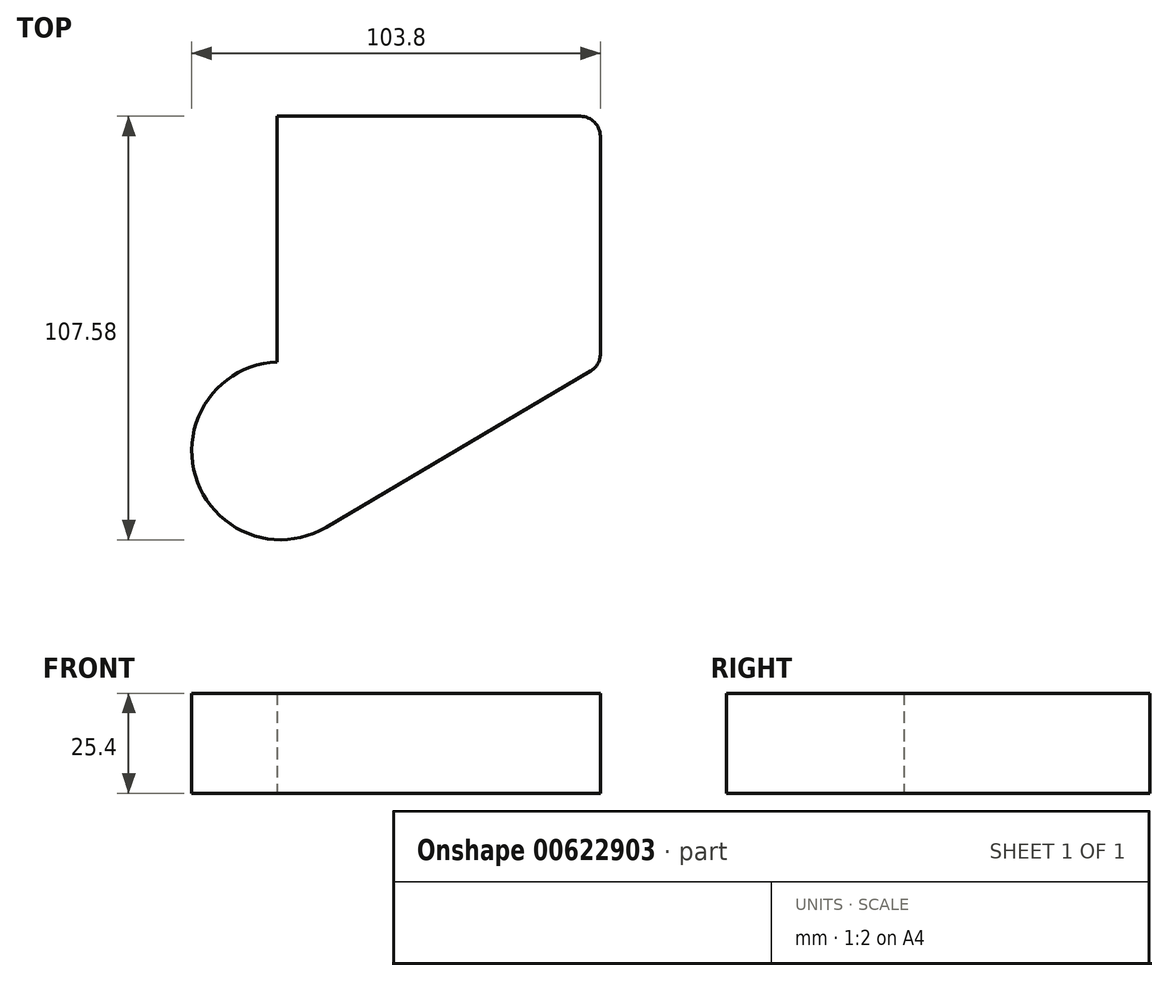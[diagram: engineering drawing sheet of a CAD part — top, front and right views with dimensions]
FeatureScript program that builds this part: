
annotation { "Feature Type Name" : "Feature", "Feature Type Description" : "" }
export const myFeature = defineFeature(function(context is Context, id is Id, definition is map)
    precondition{}
    {
        {
            var Q0;
            Q0=qCreatedBy(makeId("Top.planeOp"),FACE);
            var sketch = newSketch(context, id + "F0", { "sketchPlane" : qUnion([Q0])});
            skArc(sketch, "E0", {"start": v(-36.11, -21.34) * mm, "mid": v(-56.84, -50.32) * mm, "end": v(-23.68, -63.36) * mm});
            skLineSegment(sketch, "E1", {"start": v(-36.11, -21.34) * mm, "end": v(-36.11, 41.08) * mm});
            skLineSegment(sketch, "E2", {"start": v(-36.11, 41.08) * mm, "end": v(46.03, 41.08) * mm});
            skLineSegment(sketch, "E3", {"start": v(46.03, 41.08) * mm, "end": v(46.03, -22.2) * mm});
            skLineSegment(sketch, "E4", {"start": v(46.03, -22.2) * mm, "end": v(-23.68, -63.36) * mm});
            skSolve(sketch);
        }
        {
            var Q0;
            Q0=makeQuery(id+"F0.imprint","IMPRINT",FACE,{"disambiguationData":[TD([[makeQuery(id+"F0.imprint","IMPRINT",EDGE,{"derivedFrom":sQuery(id+"F0.wireOp",EDGE,"E0")}),1.0]])]});
            extrude(context, id + "F1", {"entities" : qUnion([Q0]), "depth" : 25.4 * mm, "offsetDistance" : 25.4 * mm});
        }
        {
            var Q0;
            Q0=makeQuery(id+"F1.opExtrude","SWEPT_EDGE",EDGE,{"disambiguationData":[OSD([sQuery(id+"F0.wireOp",EDGE,"E3"),sQuery(id+"F0.wireOp",EDGE,"E4")])]});
            fillet(context, id + "F2", {"entities" : qUnion([Q0]), "radius" : 5.08 * mm, "tangentPropagation" : true, "allowEdgeOverflow" : false});
        }
        {
            var Q0;
            Q0=makeQuery(id+"F1.opExtrude","SWEPT_EDGE",EDGE,{"disambiguationData":[OSD([sQuery(id+"F0.wireOp",EDGE,"E2"),sQuery(id+"F0.wireOp",EDGE,"E3")])]});
            fillet(context, id + "F3", {"entities" : qUnion([Q0]), "radius" : 5.08 * mm, "tangentPropagation" : true, "allowEdgeOverflow" : false});
        }
    });
